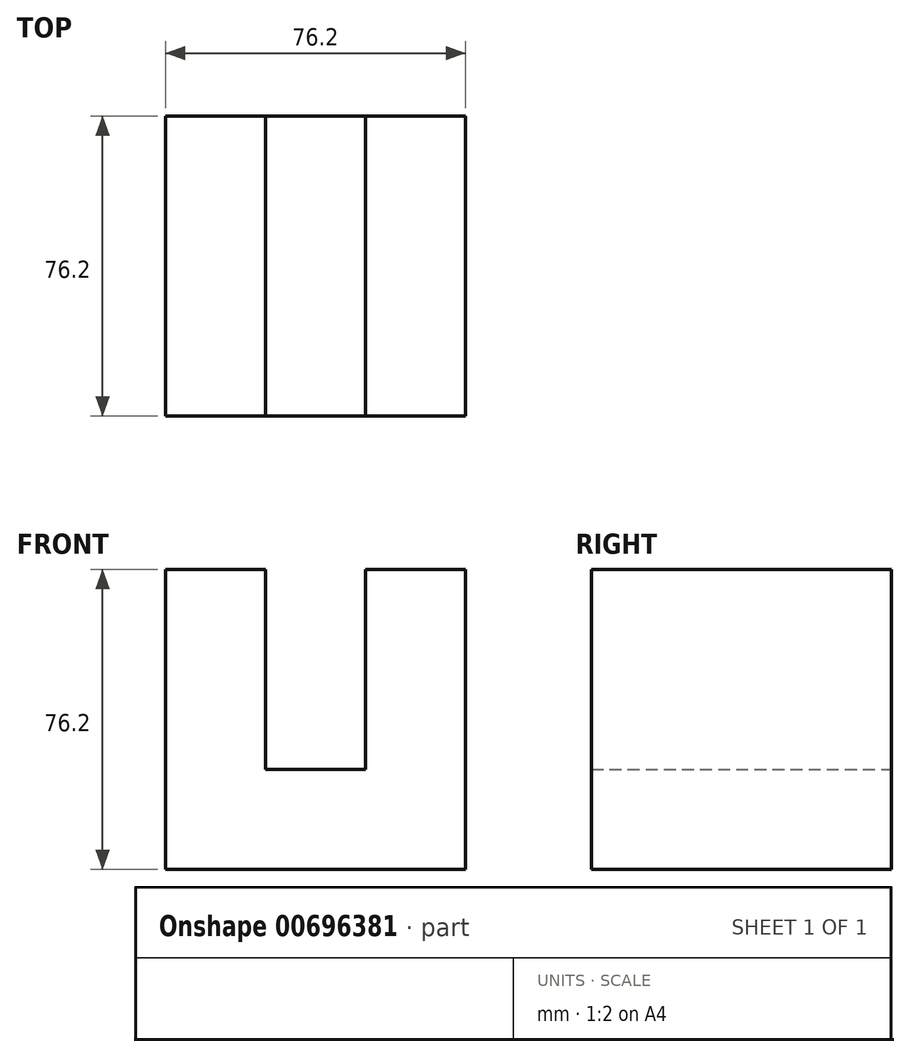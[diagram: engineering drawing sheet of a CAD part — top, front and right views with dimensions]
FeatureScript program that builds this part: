
annotation { "Feature Type Name" : "Feature", "Feature Type Description" : "" }
export const myFeature = defineFeature(function(context is Context, id is Id, definition is map)
    precondition{}
    {
        {
            var Q0;
            Q0=qCreatedBy(makeId("Front.planeOp"),FACE);
            var sketch = newSketch(context, id + "F0", { "sketchPlane" : qUnion([Q0])});
            skLineSegment(sketch, "E0.bottom", {"start": v(0, 0) * mm, "end": v(-76.2, 0) * mm});
            skLineSegment(sketch, "E0.top", {"start": v(0, 76.2) * mm, "end": v(-25.4, 76.2) * mm});
            skLineSegment(sketch, "E0.left", {"start": v(0, 0) * mm, "end": v(0, 76.2) * mm});
            skLineSegment(sketch, "E0.right", {"start": v(-76.2, 0) * mm, "end": v(-76.2, 76.2) * mm});
            skLineSegment(sketch, "E1.top", {"start": v(-50.8, 25.4) * mm, "end": v(-25.4, 25.4) * mm});
            skLineSegment(sketch, "E1.left", {"start": v(-50.8, 76.2) * mm, "end": v(-50.8, 25.4) * mm});
            skLineSegment(sketch, "E1.right", {"start": v(-25.4, 76.2) * mm, "end": v(-25.4, 25.4) * mm});
            skLineSegment(sketch, "E2.trimOffspring", {"start": v(-50.8, 76.2) * mm, "end": v(-76.2, 76.2) * mm});
            skSolve(sketch);
        }
        {
            var Q0;
            Q0=makeQuery(id+"F0.imprint","IMPRINT",FACE,{"disambiguationData":[TD([[makeQuery(id+"F0.imprint","IMPRINT",EDGE,{"derivedFrom":sQuery(id+"F0.wireOp",EDGE,"E0.bottom")}),-1.0]])]});
            extrude(context, id + "F1", {"entities" : qUnion([Q0]), "depth" : 76.2 * mm, "offsetDistance" : 25.4 * mm});
        }
    });
